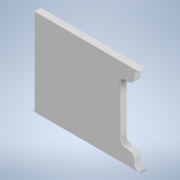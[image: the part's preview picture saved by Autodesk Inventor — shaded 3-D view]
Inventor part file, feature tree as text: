
AUTODESK INVENTOR PART (.ipt)
format: ipt  version: 2020 (Build 240168000, 168)  size: 141,824 bytes
history: native  units: in
note: dims shown in document units (in); Inventor stores cm internally (conversion verified against a paired STEP export)
features: other x4, extrude x2, sketch x2, reference x2, fillet x1, projected_geometry x1
ambient origin geometry x8: Origin, YZ Plane, XZ Plane, XY Plane, X Axis, Y Axis, Z Axis, Center Point
bodies: Solid1 (feature_tree)
feature tree (12):
  extrude  "Extrusion1"  Depth=0.125in
  fillet  "Fillet1"  Radius=0.25in
  extrude  "Extrusion2"  [1 undecoded]
  sketch  "Sketch1"  dims[d0=0.25in d1=0.0in d2=0.125in d3=0.25in d4=0.0in]
  reference  "Reference1"
  reference  "Reference2"
  sketch  "Sketch2"
  projected_geometry  "Projected Loop1"
  other  "<userpath>\Desktop\PnP Machine\PnP Machine.iam"
  other  "PnP Machine.iam"
  other  "ST8918L4508-A:1"
  other  "Corner Stand Extension:1"
note: 1 required parameter value undecoded (feature->parameter linkage not recoverable at this tier; creation-order binding heuristic only, values carry confidence <= 0.55)
